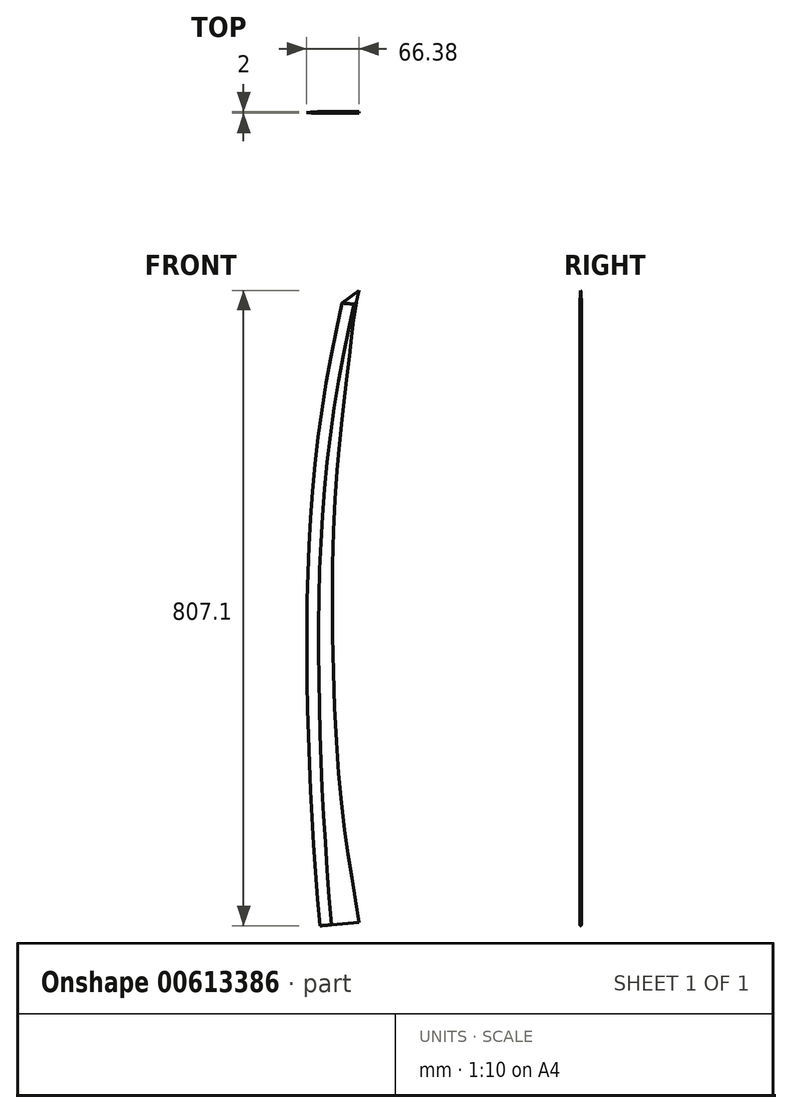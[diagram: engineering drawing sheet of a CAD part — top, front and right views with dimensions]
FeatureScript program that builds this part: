
annotation { "Feature Type Name" : "Feature", "Feature Type Description" : "" }
export const myFeature = defineFeature(function(context is Context, id is Id, definition is map)
    precondition{}
    {
        {
            var Q0;
            Q0=qCreatedBy(makeId("Front.planeOp"),FACE);
            var sketch = newSketch(context, id + "F0", { "sketchPlane" : qUnion([Q0])});
            skFitSpline(sketch, "E0", {"points": [v(-50.72, -412.76) * mm, v(-61.82, 116.73) * mm, v(-22.6, 378.23) * mm], "startDerivative": vector(-85.45, 980.91) * mm, "endDerivative": vector(123.55, 575.3) * mm});
            skLineSegment(sketch, "E1", {"start": v(-22.6, 378.23) * mm, "end": v(-0.9, 394.34) * mm});
            skFitSpline(sketch, "E2", {"points": [v(-0.9, 394.34) * mm, v(-14.66, 298.33) * mm, v(-31.84, 117.67) * mm, v(-25.93, -228.17) * mm, v(-0.9, -408.53) * mm], "startDerivative": vector(-124.77, -508.66) * mm, "endDerivative": vector(104.78, -659.2) * mm});
            skLineSegment(sketch, "E3", {"start": v(-50.72, -412.76) * mm, "end": v(-0.9, -408.53) * mm});
            skSolve(sketch);
        }
        {
            var Q0;
            Q0 = qSketchRegion(id + "F0", true);
            extrude(context, id + "F1", {"entities" : qUnion([Q0]), "endBound" : BoundingType.SYMMETRIC, "depth" : 2 * mm, "offsetDistance" : 25 * mm});
        }
        {
            var Q0;
            Q0=makeQuery(id+"F1.opExtrude","CAP_EDGE",EDGE,{"disambiguationData":[OSD([sQuery(id+"F0.wireOp",EDGE,"E0")])],"isStart":false});
            chamfer(context, id + "F2", {"entities" : qUnion([Q0]), "chamferType" : ChamferType.TWO_OFFSETS, "width1" : 1 * mm, "oppositeDirection" : false, "width2" : 15 * mm, "tangentPropagation" : true});
        }
        {
            var Q0;
            Q0=makeQuery(id+"F1.opExtrude","CAP_EDGE",EDGE,{"disambiguationData":[OSD([sQuery(id+"F0.wireOp",EDGE,"E0")])],"isStart":true});
            chamfer(context, id + "F3", {"entities" : qUnion([Q0]), "chamferType" : ChamferType.TWO_OFFSETS, "width1" : 15 * mm, "oppositeDirection" : false, "width2" : 1 * mm, "tangentPropagation" : true});
        }
        {
            var Q0;
            Q0=makeQuery(id+"F1.opExtrude","CAP_EDGE",EDGE,{"disambiguationData":[OSD([sQuery(id+"F0.wireOp",EDGE,"E1")])],"isStart":true});
            chamfer(context, id + "F4", {"entities" : qUnion([Q0]), "chamferType" : ChamferType.TWO_OFFSETS, "width1" : 10 * mm, "oppositeDirection" : false, "width2" : 1 * mm, "tangentPropagation" : true});
        }
        {
            var Q0;
            Q0=makeQuery(id+"F1.opExtrude","CAP_EDGE",EDGE,{"disambiguationData":[OSD([sQuery(id+"F0.wireOp",EDGE,"E1")])],"isStart":false});
            chamfer(context, id + "F5", {"entities" : qUnion([Q0]), "chamferType" : ChamferType.TWO_OFFSETS, "width1" : 1 * mm, "oppositeDirection" : false, "width2" : 10 * mm, "tangentPropagation" : true});
        }
    });
